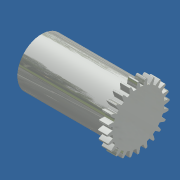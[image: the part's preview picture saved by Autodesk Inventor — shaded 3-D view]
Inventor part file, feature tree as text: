
AUTODESK INVENTOR PART (.ipt)
format: ipt  version: 2020 (Build 240168000, 168)  size: 1,576,960 bytes
history: mixed  units: mm
features: extrude x4, sketch x4, fillet x1, imported_body x1
ambient origin geometry x8: Origin, YZ Plane, XZ Plane, XY Plane, X Axis, Y Axis, Z Axis, Center Point
bodies: Solid1 (imported_parasolid)
feature tree (10):
  fillet  "Redondeo6"  Radius=1.0mm
  extrude  "Extrusion1"  Depth=4.0mm TaperAngle=0.0deg
  extrude  "Extrusion4"  Depth=5.0mm
  extrude  "Extrusion5"  Depth=2.0mm
  extrude  "Extrusion6"  Depth=4.0mm TaperAngle=0.0deg
  sketch  "Sketch1"  dims[d4=4.0mm d5=0.0mm d8=35.0mm d9=0.0mm]
  sketch  "Sketch4"  dims[d10=8.5mm d11=5.0mm]
  sketch  "Sketch5"  dims[d12=2.0mm d13=3.0mm]
  sketch  "Sketch7"  dims[d14=40.0mm d16=360.0deg d18=40.25mm d19=0.0mm d20=20.0mm d21=4.0mm d22=0.0mm]
  imported_body  NMx_Import_Brep_tag  [imported B-rep: ~23 faces, bbox_mm=[35.4, 18.513162, 15.165151]]
